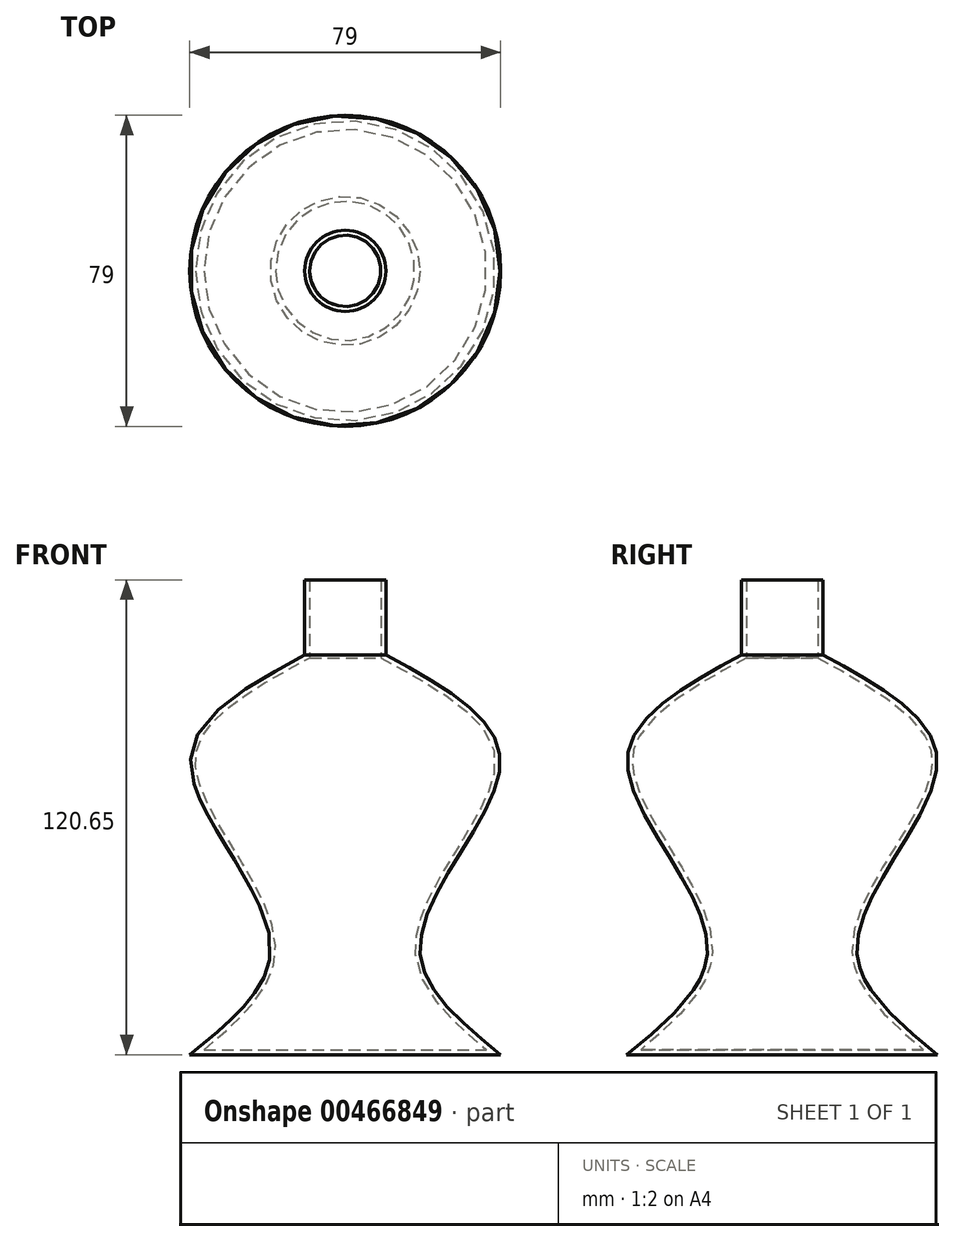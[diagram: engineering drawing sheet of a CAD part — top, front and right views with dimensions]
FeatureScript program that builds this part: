
annotation { "Feature Type Name" : "Feature", "Feature Type Description" : "" }
export const myFeature = defineFeature(function(context is Context, id is Id, definition is map)
    precondition{}
    {
        {
            var Q0;
            Q0=qCreatedBy(makeId("Top.planeOp"),FACE);
            var sketch = newSketch(context, id + "F0", { "sketchPlane" : qUnion([Q0])});
            skCircle(sketch, "E0", {"center": v(0, 0) * mm, "radius": 39.5 * mm});
            skCircle(sketch, "E1", {"center": v(0, 0) * mm, "radius": 39.88 * mm});
            skSolve(sketch);
        }
        {
            var Q0;
            Q0=qCreatedBy(makeId("Top.planeOp"),FACE);
            cPlane(context, id + "F1", {"entities" : qUnion([Q0]), "cplaneType" : CPlaneType.OFFSET, "offset" : 25.4 * mm, "width" : 152.4 * mm, "height" : 152.4 * mm});
        }
        {
            var Q0;
            Q0=qCreatedBy(id+"F1.planeOp",FACE);
            var sketch = newSketch(context, id + "F2", { "sketchPlane" : qUnion([Q0])});
            skCircle(sketch, "E2", {"center": v(0, 0) * mm, "radius": 19.03 * mm});
            skSolve(sketch);
        }
        {
            var Q0;
            Q0=qCreatedBy(id+"F1.planeOp",FACE);
            cPlane(context, id + "F3", {"entities" : qUnion([Q0]), "cplaneType" : CPlaneType.OFFSET, "offset" : 50.8 * mm, "width" : 152.4 * mm, "height" : 152.4 * mm});
        }
        {
            var Q0;
            Q0=qCreatedBy(id+"F3.planeOp",FACE);
            var sketch = newSketch(context, id + "F4", { "sketchPlane" : qUnion([Q0])});
            skCircle(sketch, "E3", {"center": v(0, 0) * mm, "radius": 39.27 * mm});
            skSolve(sketch);
        }
        {
            var Q0;
            Q0=qCreatedBy(id+"F3.planeOp",FACE);
            cPlane(context, id + "F5", {"entities" : qUnion([Q0]), "cplaneType" : CPlaneType.OFFSET, "offset" : 25.4 * mm, "width" : 152.4 * mm, "height" : 152.4 * mm});
        }
        {
            var Q0;
            Q0=qCreatedBy(id+"F5.planeOp",FACE);
            var sketch = newSketch(context, id + "F6", { "sketchPlane" : qUnion([Q0])});
            skCircle(sketch, "E4", {"center": v(0, 0) * mm, "radius": 10.32 * mm});
            skSolve(sketch);
        }
        {
            var Q0;
            Q0=makeQuery(id+"F0.imprint","IMPRINT",FACE,{"disambiguationData":[TD([[makeQuery(id+"F0.imprint","IMPRINT",EDGE,{"derivedFrom":sQuery(id+"F0.wireOp",EDGE,"E0")}),1.0]])]});
            var Q1;
            Q1=makeQuery(id+"F2.imprint","IMPRINT",FACE,{"disambiguationData":[TD([[makeQuery(id+"F2.imprint","IMPRINT",EDGE,{"derivedFrom":sQuery(id+"F2.wireOp",EDGE,"E2")}),1.0]])]});
            var Q2;
            Q2=makeQuery(id+"F4.imprint","IMPRINT",FACE,{"disambiguationData":[TD([[makeQuery(id+"F4.imprint","IMPRINT",EDGE,{"derivedFrom":sQuery(id+"F4.wireOp",EDGE,"E3")}),1.0]])]});
            var Q3;
            Q3=makeQuery(id+"F6.imprint","IMPRINT",FACE,{"disambiguationData":[TD([[makeQuery(id+"F6.imprint","IMPRINT",EDGE,{"derivedFrom":sQuery(id+"F6.wireOp",EDGE,"E4")}),1.0]])]});
            loft(context, id + "F7", {"sheetProfilesArray" : [{ "sheetProfileEntities" : qUnion([Q0]) }, { "sheetProfileEntities" : qUnion([Q1]) }, { "sheetProfileEntities" : qUnion([Q2]) }, { "sheetProfileEntities" : qUnion([Q3]) }]});
        }
        {
            var Q0;
            Q0=makeQuery(id+"F7.opLoft","CAP_FACE",FACE,{"disambiguationData":[OSD([makeQuery(id+"F6.imprint","IMPRINT",FACE,{"disambiguationData":[TD([[makeQuery(id+"F6.imprint","IMPRINT",EDGE,{"derivedFrom":sQuery(id+"F6.wireOp",EDGE,"E4")}),1.0]])]})])],"isStart":true});
            extrude(context, id + "F8", {"entities" : qUnion([Q0]), "operationType" : NewBodyOperationType.ADD, "depth" : 19.05 * mm});
        }
        {
            var Q0;
            Q0=makeQuery(id+"F8.opExtrude","CAP_FACE",FACE,{"disambiguationData":[OSD([makeQuery(id+"F6.imprint","IMPRINT",FACE,{"disambiguationData":[TD([[makeQuery(id+"F6.imprint","IMPRINT",EDGE,{"derivedFrom":sQuery(id+"F6.wireOp",EDGE,"E4")}),1.0]])]})])],"isStart":false});
            shell(context, id + "F9", {"entities" : qUnion([Q0]), "thickness" : 1.27 * mm});
        }
    });
